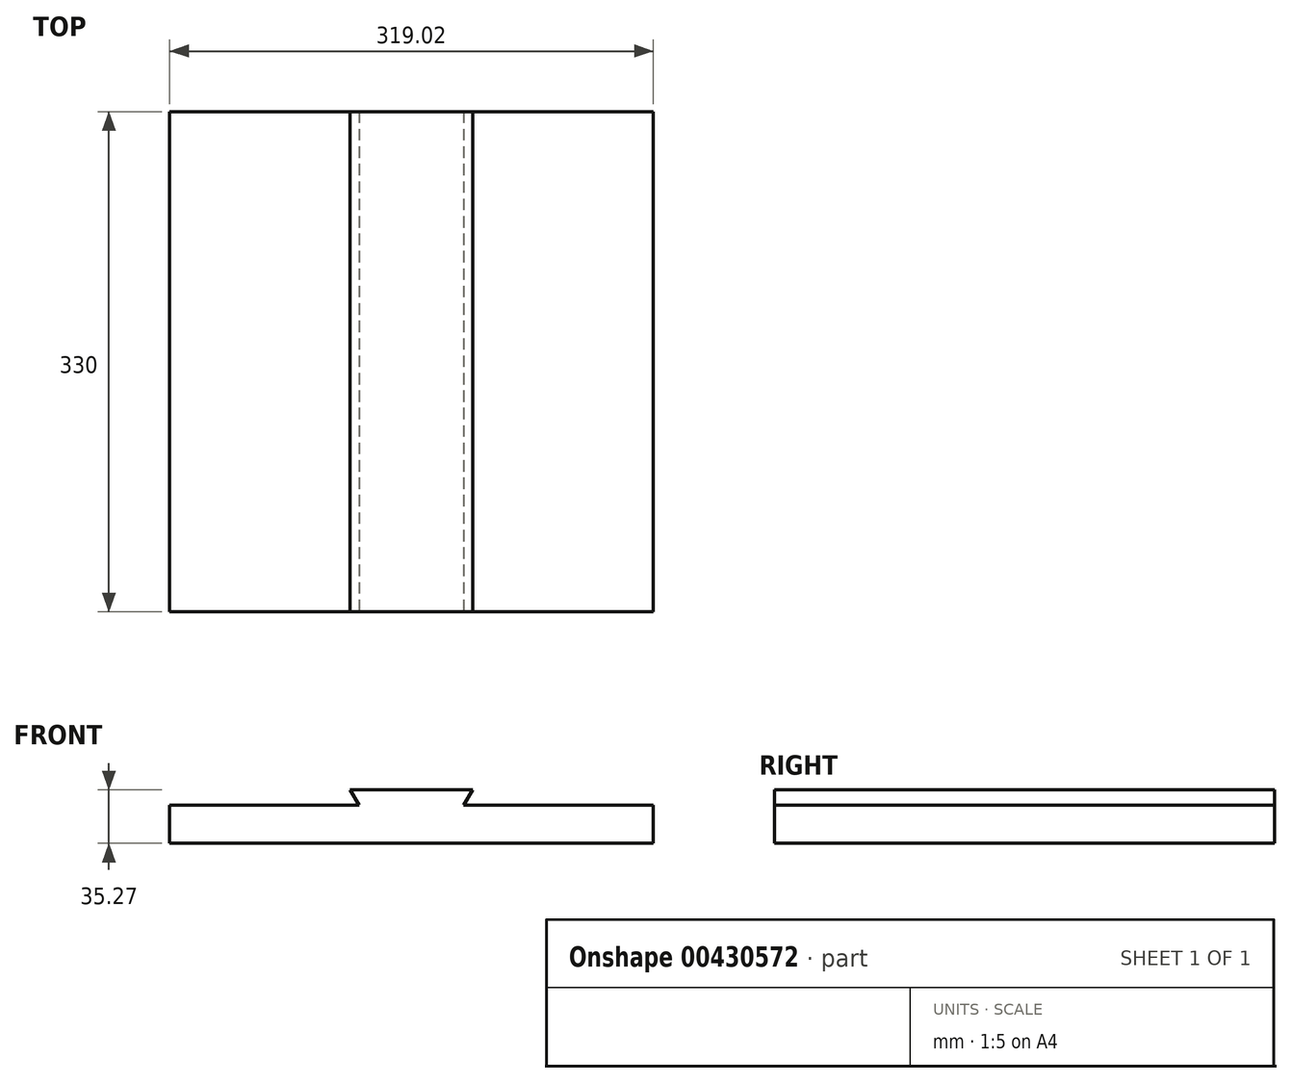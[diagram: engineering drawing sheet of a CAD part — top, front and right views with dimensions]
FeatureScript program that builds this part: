
annotation { "Feature Type Name" : "Feature", "Feature Type Description" : "" }
export const myFeature = defineFeature(function(context is Context, id is Id, definition is map)
    precondition{}
    {
        {
            var Q0;
            Q0=qCreatedBy(makeId("Front.planeOp"),FACE);
            var sketch = newSketch(context, id + "F0", { "sketchPlane" : qUnion([Q0])});
            skLineSegment(sketch, "E0", {"start": v(108.36, 0) * mm, "end": v(94.51, 0) * mm});
            skLineSegment(sketch, "E1", {"start": v(-11.64, -25) * mm, "end": v(108.36, -25) * mm});
            skLineSegment(sketch, "E2", {"start": v(25.49, 0) * mm, "end": v(19.56, 10.27) * mm});
            skLineSegment(sketch, "E3", {"start": v(19.56, 10.27) * mm, "end": v(100.44, 10.27) * mm});
            skLineSegment(sketch, "E4", {"start": v(100.44, 10.27) * mm, "end": v(94.51, 0) * mm});
            skLineSegment(sketch, "E5", {"start": v(60, 30.29) * mm, "end": v(60, -62.68) * mm, "construction": true});
            skLineSegment(sketch, "E6.trimOffspring", {"start": v(25.49, 0) * mm, "end": v(0, 0) * mm});
            skLineSegment(sketch, "E7", {"start": v(108.36, 0) * mm, "end": v(219.51, 0) * mm});
            skLineSegment(sketch, "E8", {"start": v(219.51, 0) * mm, "end": v(219.51, -25) * mm});
            skLineSegment(sketch, "E9", {"start": v(219.51, -25) * mm, "end": v(108.36, -25) * mm});
            skLineSegment(sketch, "E10", {"start": v(0, 0) * mm, "end": v(-99.51, 0) * mm});
            skLineSegment(sketch, "E11", {"start": v(-99.51, 0) * mm, "end": v(-99.51, -25) * mm});
            skLineSegment(sketch, "E12", {"start": v(-99.51, -25) * mm, "end": v(-11.64, -25) * mm});
            skSolve(sketch);
        }
        {
            var Q0;
            Q0=makeQuery(id+"F0.imprint","IMPRINT",FACE,{"disambiguationData":[TD([[makeQuery(id+"F0.imprint","IMPRINT",EDGE,{"derivedFrom":sQuery(id+"F0.wireOp",EDGE,"E0")}),1.0]])]});
            extrude(context, id + "F1", {"entities" : qUnion([Q0]), "oppositeDirection" : true, "depth" : 330 * mm});
        }
    });
